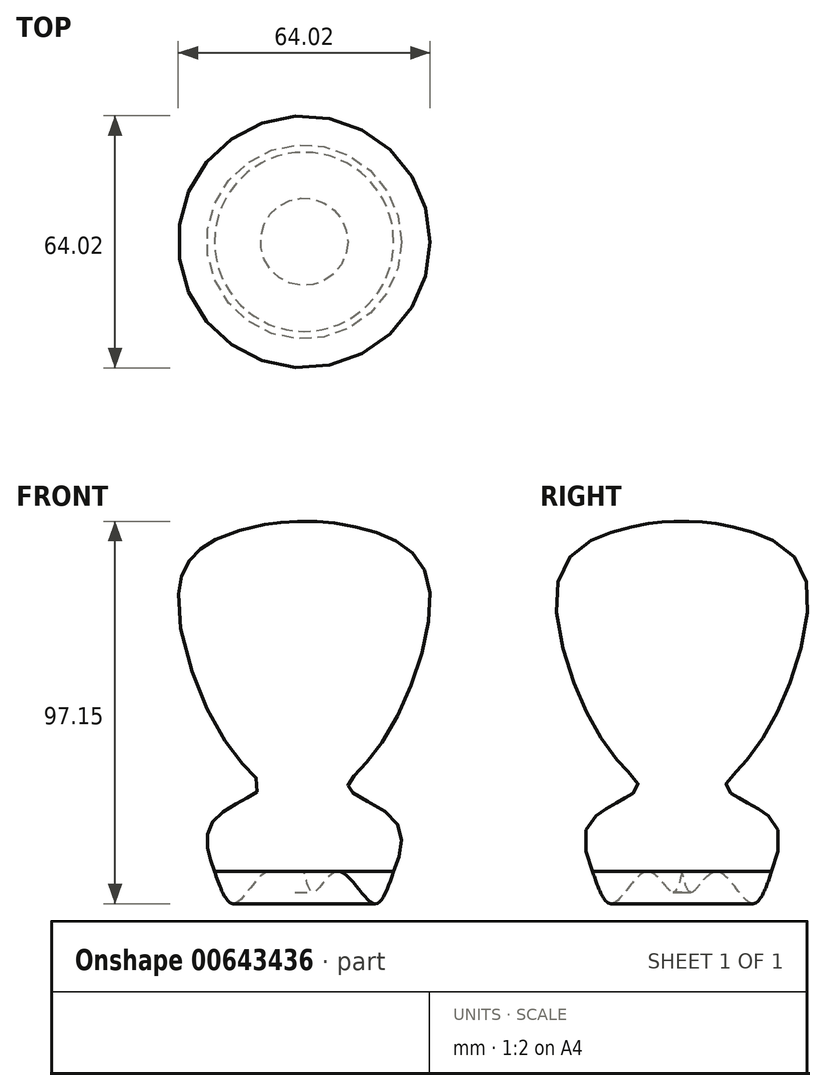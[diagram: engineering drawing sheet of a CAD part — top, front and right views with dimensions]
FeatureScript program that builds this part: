
annotation { "Feature Type Name" : "Feature", "Feature Type Description" : "" }
export const myFeature = defineFeature(function(context is Context, id is Id, definition is map)
    precondition{}
    {
        {
            var Q0;
            Q0=qCreatedBy(makeId("Front.planeOp"),FACE);
            var sketch = newSketch(context, id + "F0", { "sketchPlane" : qUnion([Q0])});
            skLineSegment(sketch, "E0", {"start": v(0, 0) * mm, "end": v(0, 88.89) * mm});
            skFitSpline(sketch, "E1", {"points": [v(22.76, 0) * mm, v(23.47, 12.4) * mm, v(11.32, 20.97) * mm, v(17.51, 29.55) * mm, v(31.56, 73.43) * mm, v(16, 86.8) * mm, v(0, 88.89) * mm], "startDerivative": vector(29.55, 76.08) * mm, "endDerivative": vector(-56.33, -6.07) * mm});
            skFitSpline(sketch, "E2", {"points": [v(22.76, 0) * mm, v(17.51, -8.1) * mm, v(8.7, 0) * mm, v(2.5, -5.24) * mm, v(0, 0) * mm], "startDerivative": vector(-17.3, -50.5) * mm, "endDerivative": vector(-9.4, 41.24) * mm});
            skSolve(sketch);
        }
        {
            var Q0;
            Q0=makeQuery(id+"F0.imprint","IMPRINT",FACE,{"disambiguationData":[TD([[makeQuery(id+"F0.imprint","IMPRINT",EDGE,{"derivedFrom":sQuery(id+"F0.wireOp",EDGE,"E0")}),-1.0]])]});
            var Q1;
            Q1=sQuery(id+"F0.wireOp",EDGE,"E1");
            var Q2;
            Q2=sQuery(id+"F0.wireOp",EDGE,"E2");
            var Q3;
            Q3=sQuery(id+"F0.wireOp",EDGE,"E0");
            revolve(context, id + "F1", {"bodyType" : ToolBodyType.SURFACE, "entities" : qUnion([Q0]), "surfaceEntities" : qUnion([Q1, Q2]), "axis" : qUnion([Q3]), "revolveType" : RevolveType.FULL});
        }
    });
